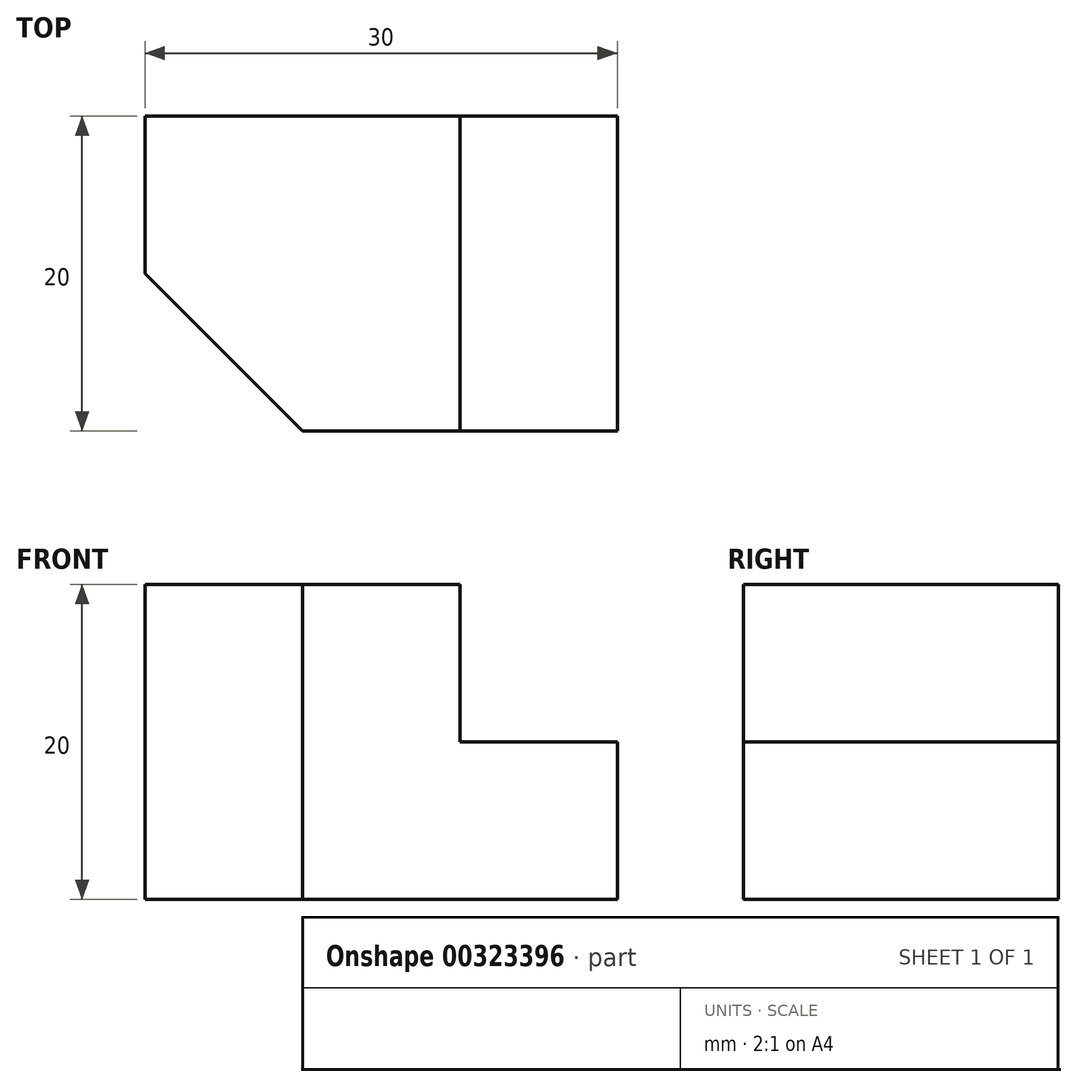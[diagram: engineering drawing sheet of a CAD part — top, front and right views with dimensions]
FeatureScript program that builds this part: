
annotation { "Feature Type Name" : "Feature", "Feature Type Description" : "" }
export const myFeature = defineFeature(function(context is Context, id is Id, definition is map)
    precondition{}
    {
        {
            var Q0;
            Q0=qCreatedBy(makeId("Front.planeOp"),FACE);
            var sketch = newSketch(context, id + "F0", { "sketchPlane" : qUnion([Q0])});
            skLineSegment(sketch, "E0.bottom", {"start": v(0, 0) * mm, "end": v(30, 0) * mm});
            skLineSegment(sketch, "E0.top", {"start": v(0, 20) * mm, "end": v(30, 20) * mm});
            skLineSegment(sketch, "E0.left", {"start": v(0, 0) * mm, "end": v(0, 20) * mm});
            skLineSegment(sketch, "E0.right", {"start": v(30, 0) * mm, "end": v(30, 20) * mm});
            skSolve(sketch);
        }
        {
            var Q0;
            Q0 = qSketchRegion(id + "F0", true);
            extrude(context, id + "F1", {"entities" : qUnion([Q0]), "depth" : 20 * mm});
        }
        {
            var Q0;
            Q0=makeQuery(id+"F1.opExtrude","CAP_FACE",FACE,{"disambiguationData":[OSD([sQuery(id+"F0.wireOp",EDGE,"E0.bottom"),sQuery(id+"F0.wireOp",EDGE,"E0.top"),sQuery(id+"F0.wireOp",EDGE,"E0.left"),sQuery(id+"F0.wireOp",EDGE,"E0.right")])],"isStart":false});
            var sketch = newSketch(context, id + "F2", { "sketchPlane" : qUnion([Q0])});
            skLineSegment(sketch, "E1.bottom", {"start": v(20, 20) * mm, "end": v(30, 20) * mm});
            skLineSegment(sketch, "E1.top", {"start": v(20, 10) * mm, "end": v(30, 10) * mm});
            skLineSegment(sketch, "E1.left", {"start": v(20, 20) * mm, "end": v(20, 10) * mm});
            skLineSegment(sketch, "E1.right", {"start": v(30, 20) * mm, "end": v(30, 10) * mm});
            skSolve(sketch);
        }
        {
            var Q0;
            Q0 = qSketchRegion(id + "F2", true);
            extrude(context, id + "F3", {"entities" : qUnion([Q0]), "operationType" : NewBodyOperationType.REMOVE, "oppositeDirection" : true, "depth" : 20 * mm});
        }
        {
            var Q0;
            Q0=makeQuery(id+"F1.opExtrude","SWEPT_FACE",FACE,{"disambiguationData":[OSD([sQuery(id+"F0.wireOp",EDGE,"E0.top")])]});
            var sketch = newSketch(context, id + "F4", { "sketchPlane" : qUnion([Q0])});
            skLineSegment(sketch, "E2", {"start": v(0, -10) * mm, "end": v(10, -20) * mm});
            skLineSegment(sketch, "E3", {"start": v(0, -20) * mm, "end": v(10, -20) * mm});
            skLineSegment(sketch, "E4", {"start": v(0, -20) * mm, "end": v(0, -10) * mm});
            skSolve(sketch);
        }
        {
            var Q0;
            Q0 = qSketchRegion(id + "F4", true);
            extrude(context, id + "F5", {"entities" : qUnion([Q0]), "operationType" : NewBodyOperationType.REMOVE, "endBound" : BoundingType.THROUGH_ALL, "oppositeDirection" : true, "depth" : 25 * mm});
        }
    });
